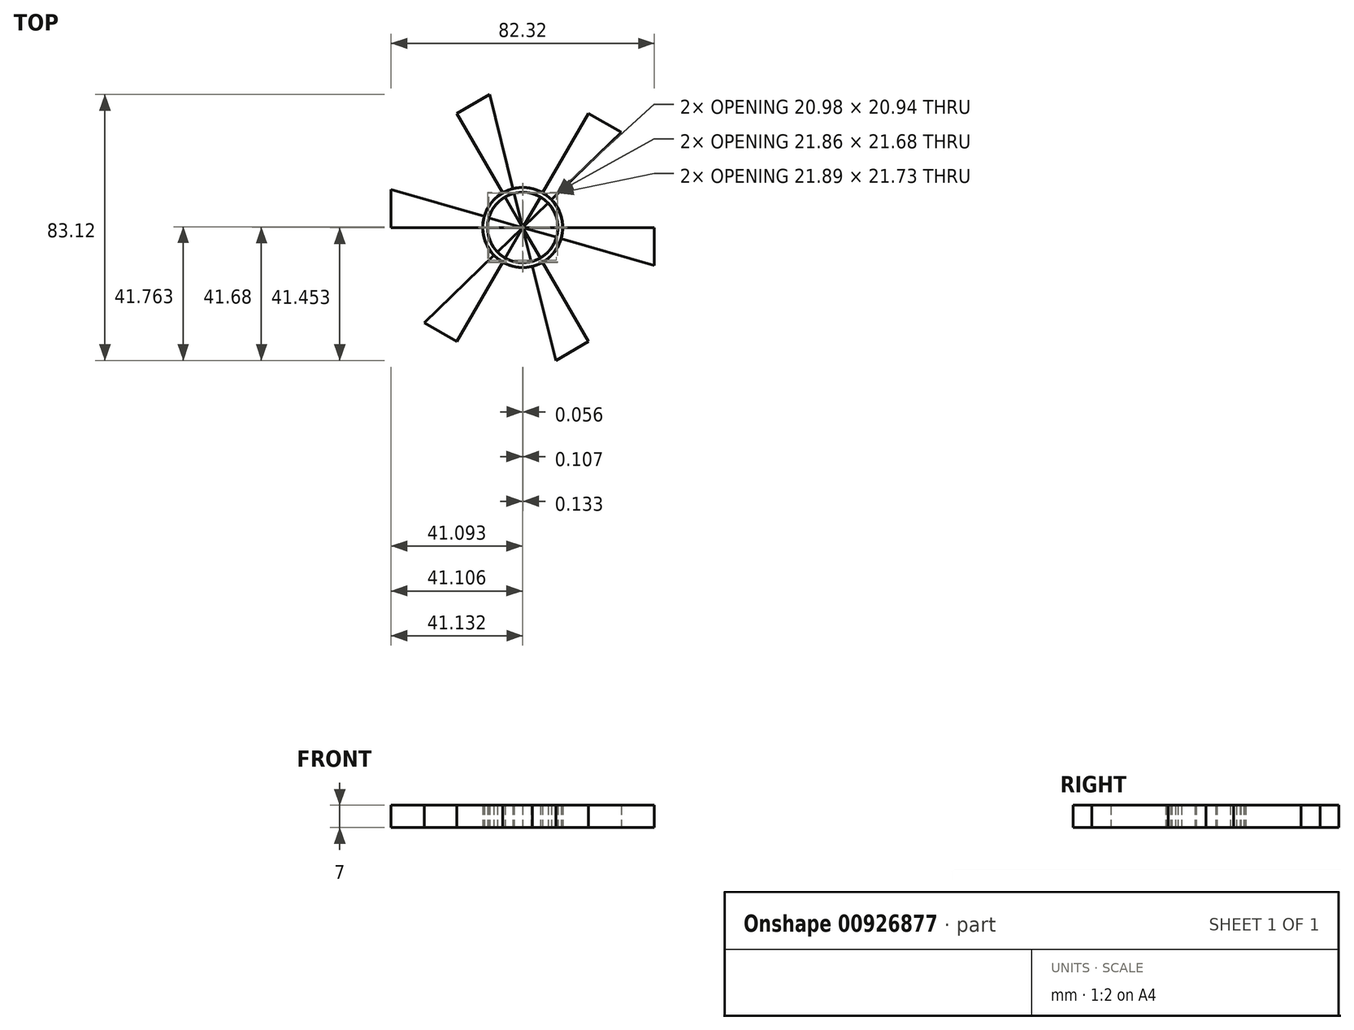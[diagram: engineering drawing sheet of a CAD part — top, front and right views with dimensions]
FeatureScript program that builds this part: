
annotation { "Feature Type Name" : "Feature", "Feature Type Description" : "" }
export const myFeature = defineFeature(function(context is Context, id is Id, definition is map)
    precondition{}
    {
        {
            var Q0;
            Q0=qCreatedBy(makeId("Top.planeOp"),FACE);
            var sketch = newSketch(context, id + "F0", { "sketchPlane" : qUnion([Q0])});
            skCircle(sketch, "E0", {"center": v(0, 0) * mm, "radius": 11 * mm});
            skCircle(sketch, "E1", {"center": v(0, 0) * mm, "radius": 12.5 * mm});
            skSolve(sketch);
        }
        {
            var Q0;
            Q0 = qSketchRegion(id + "F0", true);
            extrude(context, id + "F1", {"entities" : qUnion([Q0]), "depth" : 7 * mm, "offsetDistance" : 25.4 * mm});
        }
        {
            var Q0;
            Q0=qCreatedBy(makeId("Top.planeOp"),FACE);
            var sketch = newSketch(context, id + "F2", { "sketchPlane" : qUnion([Q0])});
            skLineSegment(sketch, "E2", {"start": v(0, 0) * mm, "end": v(41.16, 0) * mm});
            skLineSegment(sketch, "E3", {"start": v(41.16, 0) * mm, "end": v(41.16, -11.82) * mm});
            skLineSegment(sketch, "E4", {"start": v(41.16, -11.82) * mm, "end": v(0, 0) * mm});
            skSolve(sketch);
        }
        {
            var Q0;
            Q0 = qSketchRegion(id + "F2", true);
            extrude(context, id + "F3", {"entities" : qUnion([Q0]), "operationType" : NewBodyOperationType.ADD, "depth" : 7 * mm, "offsetDistance" : 25.4 * mm});
        }
        {
            var Q0;
            Q0=makeQuery(id+"F1.opExtrude","SWEPT_BODY",BODY,{"disambiguationData":[OSD([sQuery(id+"F0.wireOp",EDGE,"E0"),sQuery(id+"F0.wireOp",EDGE,"E1")])]});
            var Q1;
            Q1=makeQuery(id+"F1.opExtrude","SWEPT_FACE",FACE,{"disambiguationData":[OSD([sQuery(id+"F0.wireOp",EDGE,"E1")])]});
            circularPattern(context, id + "F4", {"entities" : qUnion([Q0]), "axis" : qUnion([Q1]), "angle" : 360 * degree, "instanceCount" : 6, "equalSpace" : true});
        }
    });
